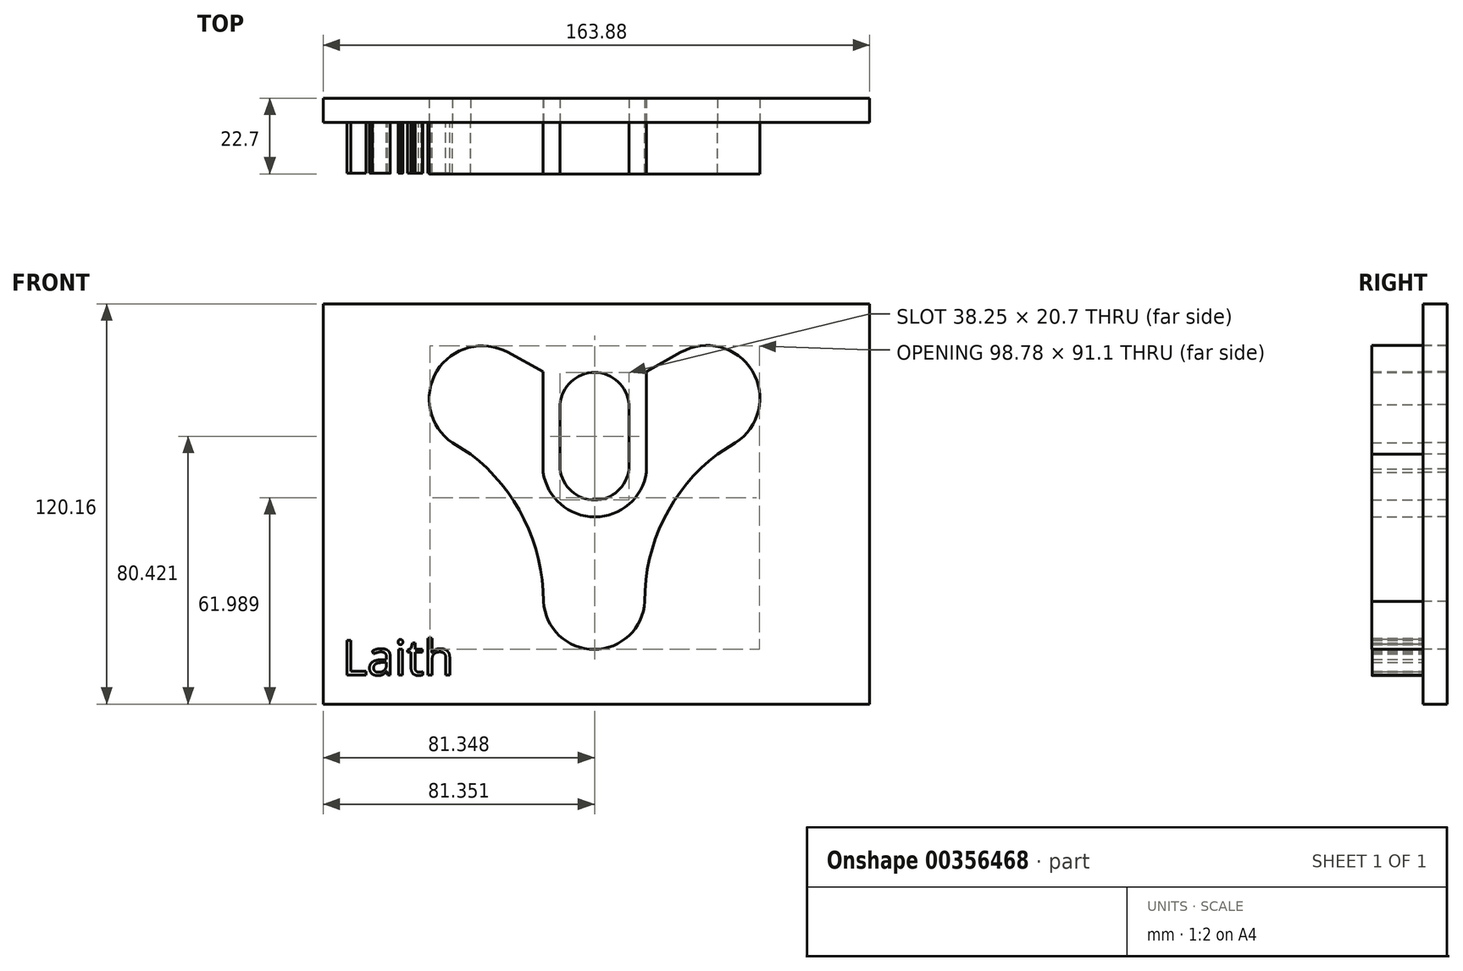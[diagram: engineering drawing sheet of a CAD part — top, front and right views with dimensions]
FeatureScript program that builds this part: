
annotation { "Feature Type Name" : "Feature", "Feature Type Description" : "" }
export const myFeature = defineFeature(function(context is Context, id is Id, definition is map)
    precondition{}
    {
        {
            var Q0;
            Q0=qCreatedBy(makeId("Front.planeOp"),FACE);
            var sketch = newSketch(context, id + "F0", { "sketchPlane" : qUnion([Q0])});
            skLineSegment(sketch, "E0", {"start": v(-10.94, 29.86) * mm, "end": v(-10.94, 10.45) * mm});
            skLineSegment(sketch, "E1", {"start": v(9.76, 29.86) * mm, "end": v(9.76, 10.45) * mm});
            skArc(sketch, "E2", {"start": v(-10.94, 10.45) * mm, "mid": v(-0.59, 1.22) * mm, "end": v(9.76, 10.45) * mm});
            skArc(sketch, "E3", {"start": v(9.76, 29.86) * mm, "mid": v(-0.59, 39.46) * mm, "end": v(-10.94, 29.86) * mm});
            skLineSegment(sketch, "E4", {"start": v(14.96, 39.72) * mm, "end": v(14.96, 9.5) * mm});
            skLineSegment(sketch, "E5", {"start": v(-16, 9.5) * mm, "end": v(-16, 39.72) * mm});
            skArc(sketch, "E6", {"start": v(-16, 9.5) * mm, "mid": v(-0.52, -3.9) * mm, "end": v(14.96, 9.5) * mm});
            skArc(sketch, "E7", {"start": v(-15.9, -29.26) * mm, "mid": v(-21.7, -4.65) * mm, "end": v(-37.7, 14.93) * mm});
            skArc(sketch, "E8", {"start": v(-15.9, -29.26) * mm, "mid": v(-0.72, -43.64) * mm, "end": v(14.46, -29.26) * mm});
            skArc(sketch, "E9", {"start": v(36.27, 14.93) * mm, "mid": v(20.15, -4.6) * mm, "end": v(14.46, -29.26) * mm});
            skLineSegment(sketch, "E10", {"start": v(14.96, 39.72) * mm, "end": v(25.29, 45.52) * mm});
            skLineSegment(sketch, "E11", {"start": v(36.27, 14.93) * mm, "end": v(41.65, 18.35) * mm});
            skLineSegment(sketch, "E12", {"start": v(-43.26, 18.35) * mm, "end": v(-37.7, 14.93) * mm});
            skLineSegment(sketch, "E13", {"start": v(-16, 39.72) * mm, "end": v(-26.58, 45.52) * mm});
            skArc(sketch, "E14", {"start": v(41.65, 18.35) * mm, "mid": v(46.72, 39.91) * mm, "end": v(25.29, 45.52) * mm});
            skArc(sketch, "E15", {"start": v(-26.58, 45.52) * mm, "mid": v(-47.86, 39.87) * mm, "end": v(-43.26, 18.35) * mm});
            skLineSegment(sketch, "E16.rect.bottom", {"start": v(-81.94, 60.08) * mm, "end": v(81.94, 60.08) * mm});
            skLineSegment(sketch, "E16.rect.top", {"start": v(-81.94, -60.08) * mm, "end": v(81.94, -60.08) * mm});
            skLineSegment(sketch, "E16.rect.left", {"start": v(-81.94, 60.08) * mm, "end": v(-81.94, -60.08) * mm});
            skLineSegment(sketch, "E16.rect.right", {"start": v(81.94, 60.08) * mm, "end": v(81.94, -60.08) * mm});
            skPoint(sketch, "E16.rect.middle", {"position": v(0, 0) * mm});
            skSolve(sketch);
        }
        {
            var Q0;
            Q0=makeQuery(id+"F0.imprint","IMPRINT",FACE,{"disambiguationData":[TD([[makeQuery(id+"F0.imprint","IMPRINT",EDGE,{"derivedFrom":sQuery(id+"F0.wireOp",EDGE,"E4")}),1.0]])]});
            var Q1;
            Q1=makeQuery(id+"F0.imprint","IMPRINT",FACE,{"disambiguationData":[TD([[makeQuery(id+"F0.imprint","IMPRINT",EDGE,{"derivedFrom":sQuery(id+"F0.wireOp",EDGE,"E0")}),1.0]])]});
            extrude(context, id + "F1", {"entities" : qUnion([Q0, Q1]), "depth" : 15.4 * mm});
        }
        {
            var Q0;
            Q0=makeQuery(id+"F0.imprint","IMPRINT",FACE,{"disambiguationData":[TD([[makeQuery(id+"F0.imprint","IMPRINT",EDGE,{"derivedFrom":sQuery(id+"F0.wireOp",EDGE,"E0")}),-1.0]])]});
            extrude(context, id + "F2", {"entities" : qUnion([Q0]), "oppositeDirection" : true, "depth" : 7.3 * mm});
        }
        {
            var Q0;
            Q0=qCreatedBy(makeId("Front.planeOp"),FACE);
            var sketch = newSketch(context, id + "F3", { "sketchPlane" : qUnion([Q0])});
            skText(sketch, "E17", { "text": "Laith", "fontName": "OpenSans-Regular.ttf"});
            const initialGuessF3  = {"E17": [-0.07632, -0.05135, 1, 0, 0.0105]};
            skSetInitialGuess(sketch, initialGuessF3);
            skSolve(sketch);
        }
        {
            var Q0;
            Q0 = qSketchRegion(id + "F3", true);
            extrude(context, id + "F4", {"entities" : qUnion([Q0]), "operationType" : NewBodyOperationType.ADD, "depth" : 15.24 * mm});
        }
    });
